# Revit family: Building-SurfaceMountingEnclosures-GEWISS-40CDK-ENCLOSURES_IP65_1X
name_source: partatom
category: Apparecchi elettrici
revit_build: Autodesk Revit 2016 (Build: 20161004_0715(x64)
units: mm (PartAtom-declared; Revit-internal decimal feet)

## family parameters
Condiviso = No
Host = Superficie
Mantenere orientamento annotazione = Sì
Numero OmniClass = 23.80.30.11.17
Punto di calcolo locali = Sì
Quota connettore circolare = Usa diametro
Taglio con vuoti quando caricato = No
Tipo di parte = Normale
Titolo OmniClass = Distribution Boards and Control Panels

## types (4) — shared parameters
Catalogue = BUILDING
Catalogue Range = 40 CDK
Colour = Grey RAL 7035
Diametro_tubazione = 30 mm  [stored 0.0984252 ft]
Dimensione modulo = 18 mm  [stored 0.0590551 ft]
Electrocod = 0321
Glow Wire Test = 650°C
H_finestratura = 45 mm  [stored 0.147638 ft]
H_quadro = 285 mm  [stored 0.935039 ft]
IDF = 20f4a23b-b4a2-4086-85cc-3dcfcb6f8bb6
IDT = 09bc94ce-5498-4c76-bae9-7f0a749fa703
IP degree = IP65
Insulation class = II (according to IEC 61140 standards)
Insulation voltage: = 1000 V according to EN 62208 both in ac as well as in dc
L_finestratura = 324 mm  [stored 1.06299 ft]
L_quadro = 410 mm  [stored 1.34514 ft]
N.M. = 18
Operating temperature = -25 +60 °C
Produttore = GEWISS S.p.A.
Prondita_quadro = 140 mm  [stored 0.459318 ft]
Prospetto di default = 1219 mm
Rated current: = 125A
Rated insulation voltage (Ui) = 1000 V
Rated voltage = 400V
SEO = Enclosure
Shock resistance = IK09
Sportello = Sportello_trasparente
Spostamento_Y = 560 mm
Standard = EN 60670-1 (CEI 23-48) IEC60670-24 CEI 23-49
Standard. = EN 60670-1 (CEI 23-48) IEC60670-24 CEI 23-49
Technical sheet = https://www.gewiss.com
Thermo-pressure with ball = 70
Type of material = Halogen-free in compliance with EN 60754-2
URL = https://www.gewiss.com
Version file RFA = 18.0
fase1 = 0 VA
h_sportello = 225 mm  [stored 0.738189 ft]
s = 262 mm
voltaggio_quadro = 0 V

## per-type parameters (varying)
| type | Accessories for insulation restoring | Descrizione | Dispersible power (W) | Door colour | EAN code | Insulation voltage | Max. installable terminal blocks | Modello | No. of modules EN 50022 | No. of modules EN 50022: | Outer dim. LxHxD (mm) |
| GW40102 - SUR. MOU. ENCLOSURE 8M.IP65 | Screwcaps (GW44623) or fixing brackets in resin (GW44621) | SUR. MOU. ENCLOSURE 8M.IP65 | 16 | Smoked Transparent | 8011564061514 |  | 1 x 8 modules | GW40102 | 8 | 8 | 215x210x100 |
| GW40103 - SUR. MOU. ENCLOSURE 12M.IP65 | Screwcaps (GW44623) or fixing brackets in resin (GW44621) | SUR. MOU. ENCLOSURE 12M.IP65 | 26 | Smoked Transparent | 8011564061545 |  | 1 x 12 modules | GW40103 | 12 | 12 | 298x260x140 |
| GW40106 - SUR. MOU. ENCLOSURE 18M.IP65 | Screwcaps (GW44623) or fixing brackets in resin (GW44621) | SUR. MOU. ENCLOSURE 18M.IP65 | 38 | Smoked Transparent | 8011564061576 |  | 1 x 18 modules | GW40106 | 18 | 18 | 410x285x140 |
| GW40101 - SUR. MOU. ENCLOSURE 4M.IP65 |  | SUR. MOU. ENCLOSURE 4M.IP65 | 13 |  | 8011564061477 | 1000V |  | GW40101 | 4 | 4 | 143x210x100 |

note: source unit labels omitted for Thermo-pressure with ball — the stored unit's dimension contradicts the parameter name (converter mislabeling)

note: [stored X ft] marks values corroborated as IEEE doubles in the binary element streams (Revit-internal decimal feet)

## geometry (parser evidence)
native form markers: Sweep x1
no freeform markers — native parametric forms only
